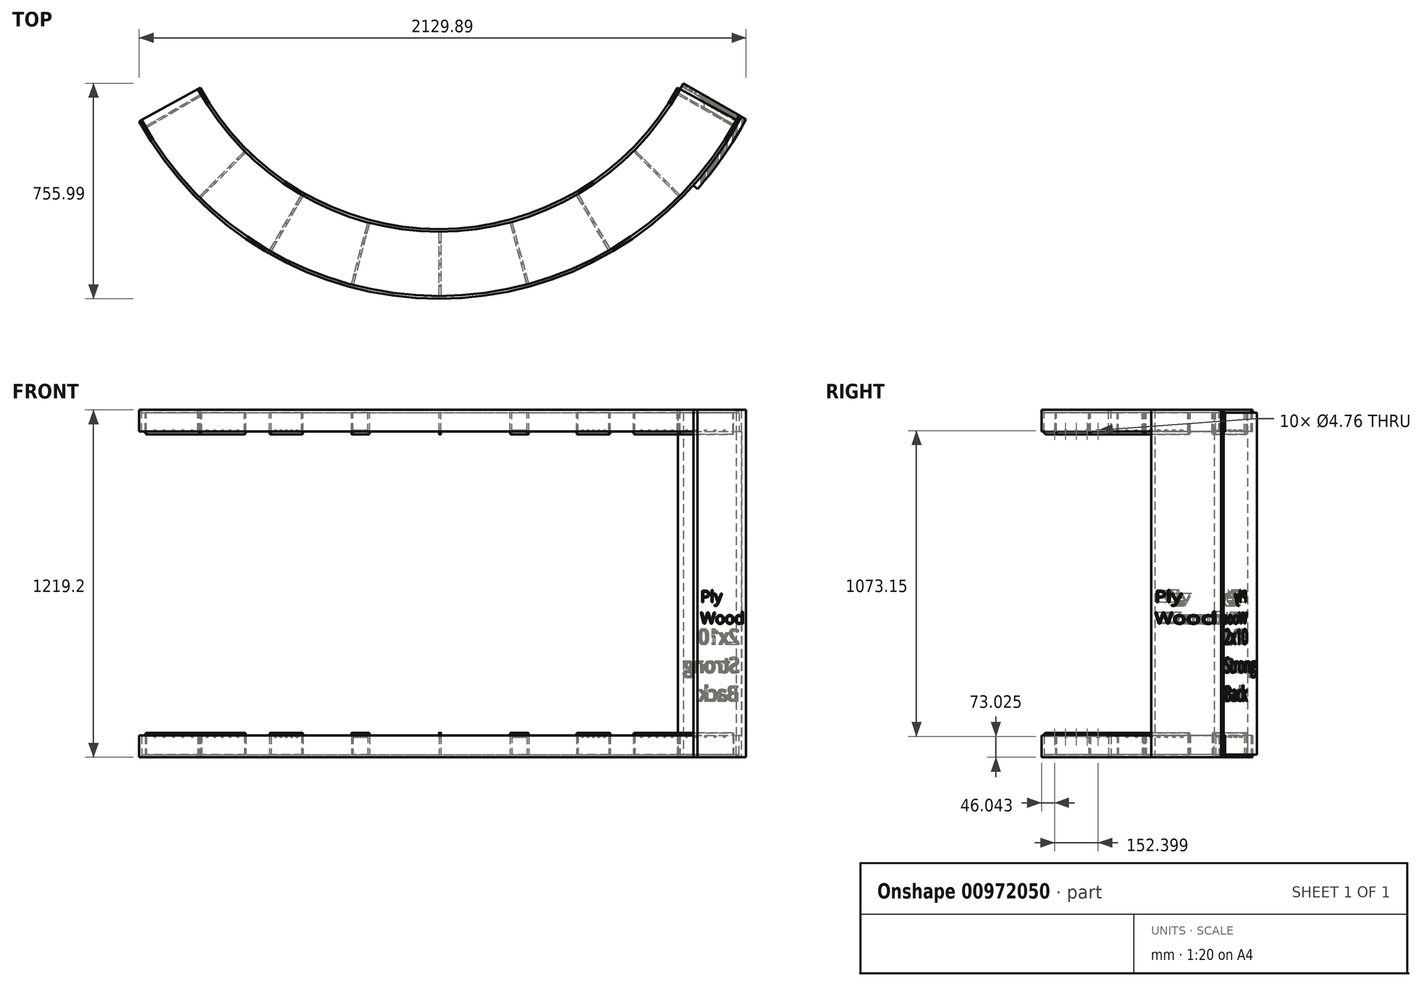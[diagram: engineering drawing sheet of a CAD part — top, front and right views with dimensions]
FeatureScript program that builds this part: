
annotation { "Feature Type Name" : "Feature", "Feature Type Description" : "" }
export const myFeature = defineFeature(function(context is Context, id is Id, definition is map)
    precondition{}
    {
        {
            var Q0;
            Q0=qCreatedBy(makeId("Top.planeOp"),FACE);
            var sketch = newSketch(context, id + "F0", { "sketchPlane" : qUnion([Q0])});
            skCircle(sketch, "E0", {"center": v(0, 0) * mm, "radius": 1190.62 * mm});
            skCircle(sketch, "E1.0", {"center": v(0, 0) * mm, "radius": 965.2 * mm});
            skLineSegment(sketch, "E2", {"start": v(-1043.85, -572.68) * mm, "end": v(0, 0) * mm});
            skLineSegment(sketch, "E3", {"start": v(0, 0) * mm, "end": v(0, -1190.62) * mm, "construction": true});
            skLineSegment(sketch, "E4.MirrorCS", {"start": v(1043.85, -572.68) * mm, "end": v(0, 0) * mm});
            skSolve(sketch);
        }
        {
            var Q0;
            {var subQ0=sQuery(id+"F0.wireOp",EDGE,"E2");var subQ1=sQuery(id+"F0.wireOp",EDGE,"E0");var subQ2=makeQuery(id+"F0.imprint","INTERSECT",VERTEX,{"derivedFrom":[subQ1,subQ0]});Q0=makeQuery(id+"F0.imprint","IMPRINT",FACE,{"disambiguationData":[TD([[makeQuery(id+"F0.imprint","IMPRINT",EDGE,{"disambiguationData":[TD([[subQ2,-1.0]])],"derivedFrom":subQ1}),1.0]])]});}
            extrude(context, id + "F1", {"entities" : qUnion([Q0]), "depth" : 9.52 * mm, "offsetDistance" : 25.4 * mm});
        }
        {
            var Q0;
            Q0=qCreatedBy(makeId("Top.planeOp"),FACE);
            var sketch = newSketch(context, id + "F2", { "sketchPlane" : qUnion([Q0])});
            skArc(sketch, "E5.0", {"start": v(-1043.85, -572.68) * mm, "mid": v(0, -1190.62) * mm, "end": v(1043.85, -572.68) * mm});
            skArc(sketch, "E6.0", {"start": v(-1052.2, -577.26) * mm, "mid": v(0, -1200.15) * mm, "end": v(1052.2, -577.26) * mm});
            skLineSegment(sketch, "E7", {"start": v(-1043.85, -572.68) * mm, "end": v(-1052.2, -577.26) * mm});
            skLineSegment(sketch, "E8", {"start": v(1052.2, -577.26) * mm, "end": v(1043.85, -572.68) * mm});
            skSolve(sketch);
        }
        {
            var Q0;
            Q0 = qSketchRegion(id + "F2", true);
            extrude(context, id + "F3", {"entities" : qUnion([Q0]), "depth" : 76.2 * mm, "offsetDistance" : 25.4 * mm});
        }
        {
            var Q0;
            Q0=qCreatedBy(makeId("Top.planeOp"),FACE);
            var sketch = newSketch(context, id + "F4", { "sketchPlane" : qUnion([Q0])});
            skArc(sketch, "E9.0", {"start": v(-846.22, -464.25) * mm, "mid": v(0, -965.2) * mm, "end": v(846.22, -464.25) * mm});
            skArc(sketch, "E10.0", {"start": v(-837.87, -459.67) * mm, "mid": v(0, -955.68) * mm, "end": v(837.87, -459.67) * mm});
            skLineSegment(sketch, "E11", {"start": v(-846.22, -464.25) * mm, "end": v(-837.87, -459.67) * mm});
            skLineSegment(sketch, "E12", {"start": v(846.22, -464.25) * mm, "end": v(837.87, -459.67) * mm});
            skSolve(sketch);
        }
        {
            var Q0;
            Q0 = qSketchRegion(id + "F4", true);
            extrude(context, id + "F5", {"entities" : qUnion([Q0]), "depth" : 76.2 * mm, "offsetDistance" : 25.4 * mm});
        }
        {
            var Q0;
            Q0=makeQuery(id+"F1.opExtrude","CAP_FACE",FACE,{"disambiguationData":[OSD([sQuery(id+"F0.wireOp",EDGE,"E0"),sQuery(id+"F0.wireOp",EDGE,"E1.0"),sQuery(id+"F0.wireOp",EDGE,"E2"),sQuery(id+"F0.wireOp",EDGE,"E4.MirrorCS")])],"isStart":false});
            var sketch = newSketch(context, id + "F6", { "sketchPlane" : qUnion([Q0])});
            skLineSegment(sketch, "E13", {"start": v(838.98, -477.21) * mm, "end": v(1034.56, -589.3) * mm});
            skLineSegment(sketch, "E14", {"start": v(1034.56, -589.3) * mm, "end": v(1031.4, -594.82) * mm});
            skLineSegment(sketch, "E15", {"start": v(1031.4, -594.82) * mm, "end": v(835.82, -482.72) * mm});
            skLineSegment(sketch, "E16", {"start": v(835.82, -482.72) * mm, "end": v(838.98, -477.21) * mm});
            skLineSegment(sketch, "E17", {"start": v(837.4, -479.97) * mm, "end": v(1032.98, -592.06) * mm, "construction": true});
            skSolve(sketch);
        }
        {
            var Q0;
            Q0 = qSketchRegion(id + "F6", true);
            extrude(context, id + "F7", {"entities" : qUnion([Q0]), "depth" : 76.2 * mm, "offsetDistance" : 25.4 * mm});
        }
        {
            var Q0;
            Q0=makeQuery(id+"F1.opExtrude","CAP_FACE",FACE,{"disambiguationData":[OSD([sQuery(id+"F0.wireOp",EDGE,"E0"),sQuery(id+"F0.wireOp",EDGE,"E1.0"),sQuery(id+"F0.wireOp",EDGE,"E2"),sQuery(id+"F0.wireOp",EDGE,"E4.MirrorCS")])],"isStart":false});
            var sketch = newSketch(context, id + "F8", { "sketchPlane" : qUnion([Q0])});
            skLineSegment(sketch, "E18.0", {"start": v(857.93, -444.16) * mm, "end": v(1061.77, -560.99) * mm});
            skLineSegment(sketch, "E19.0", {"start": v(838.98, -477.21) * mm, "end": v(1042.82, -594.04) * mm});
            skLineSegment(sketch, "E20", {"start": v(838.98, -477.21) * mm, "end": v(857.93, -444.16) * mm});
            skPoint(sketch, "E21.orphan", {"position": v(1034.56, -589.3) * mm});
            skLineSegment(sketch, "E22", {"start": v(1042.82, -594.04) * mm, "end": v(1061.77, -560.99) * mm});
            skSolve(sketch);
        }
        {
            var Q0;
            Q0 = qSketchRegion(id + "F8", true);
            extrude(context, id + "F9", {"entities" : qUnion([Q0]), "depth" : 1200.15 * mm, "offsetDistance" : 25.4 * mm});
        }
        {
            var Q0;
            Q0=makeQuery(id+"F9.opExtrude","SWEPT_FACE",FACE,{"disambiguationData":[OSD([sQuery(id+"F8.wireOp",EDGE,"E18.0")])]});
            var sketch = newSketch(context, id + "F10", { "sketchPlane" : qUnion([Q0])});
            skLineSegment(sketch, "E23.bottom", {"start": v(-1200.15, 9.53) * mm, "end": v(-1190.42, 9.53) * mm});
            skLineSegment(sketch, "E23.top", {"start": v(-1200.15, 76.2) * mm, "end": v(-1190.42, 76.2) * mm});
            skLineSegment(sketch, "E23.left", {"start": v(-1200.15, 9.52) * mm, "end": v(-1200.15, 76.2) * mm});
            skLineSegment(sketch, "E23.right", {"start": v(-1190.42, 9.53) * mm, "end": v(-1190.42, 76.2) * mm});
            skLineSegment(sketch, "E24", {"start": v(-1200.15, 609.6) * mm, "end": v(-965.2, 609.6) * mm, "construction": true});
            skLineSegment(sketch, "E25.MirrorCS", {"start": v(-1200.15, 1209.68) * mm, "end": v(-1190.42, 1209.68) * mm});
            skLineSegment(sketch, "E26.MirrorCS", {"start": v(-1200.15, 1143) * mm, "end": v(-1190.42, 1143) * mm});
            skLineSegment(sketch, "E27.MirrorCS", {"start": v(-1200.15, 1209.68) * mm, "end": v(-1200.15, 1143) * mm});
            skLineSegment(sketch, "E28.MirrorCS", {"start": v(-1190.42, 1209.68) * mm, "end": v(-1190.42, 1143) * mm});
            skSolve(sketch);
        }
        {
            var Q0;
            Q0 = qSketchRegion(id + "F10", true);
            var Q1;
            Q1=makeQuery(id+"F9.opExtrude","SWEPT_FACE",FACE,{"disambiguationData":[OSD([sQuery(id+"F8.wireOp",EDGE,"E19.0")])]});
            extrude(context, id + "F11", {"entities" : qUnion([Q0]), "operationType" : NewBodyOperationType.REMOVE, "endBound" : BoundingType.UP_TO_SURFACE, "oppositeDirection" : true, "depth" : 25.4 * mm, "endBoundEntityFace" : qUnion([Q1]), "offsetDistance" : 25.4 * mm});
        }
        {
            var Q0;
            Q0=makeQuery(id+"F7.opExtrude","CAP_EDGE",EDGE,{"disambiguationData":[OSD([sQuery(id+"F6.wireOp",EDGE,"E14")])],"isStart":false});
            var Q1;
            Q1=makeQuery(id+"F7.opExtrude","CAP_EDGE",EDGE,{"disambiguationData":[OSD([sQuery(id+"F6.wireOp",EDGE,"E16")])],"isStart":false});
            fillet(context, id + "F12", {"entities" : qUnion([Q0, Q1]), "radius" : 6.35 * mm, "tangentPropagation" : true, "allowEdgeOverflow" : false});
        }
        {
            var Q0;
            Q0=makeQuery(id+"F7.opExtrude","SWEPT_FACE",FACE,{"disambiguationData":[OSD([sQuery(id+"F6.wireOp",EDGE,"E13")])]});
            var sketch = newSketch(context, id + "F13", { "sketchPlane" : qUnion([Q0])});
            skCircle(sketch, "E29", {"center": v(-1154.11, 73.03) * mm, "radius": 2.38 * mm});
            skCircle(sketch, "E30", {"center": v(-1116.01, 73.03) * mm, "radius": 2.38 * mm});
            skCircle(sketch, "E31", {"center": v(-1039.81, 73.03) * mm, "radius": 2.38 * mm});
            skCircle(sketch, "E32", {"center": v(-1001.71, 73.03) * mm, "radius": 2.38 * mm});
            skLineSegment(sketch, "E33", {"start": v(-1154.11, 73.02) * mm, "end": v(-1116.01, 73.02) * mm, "construction": true});
            skLineSegment(sketch, "E34", {"start": v(-1039.81, 73.02) * mm, "end": v(-1001.71, 73.02) * mm, "construction": true});
            skLineSegment(sketch, "E35", {"start": v(-1077.91, 73.03) * mm, "end": v(-1077.91, 85.73) * mm, "construction": true});
            skCircle(sketch, "E36", {"center": v(-1077.91, 73.03) * mm, "radius": 2.38 * mm});
            skLineSegment(sketch, "E37", {"start": v(-1116.01, 73.03) * mm, "end": v(-1077.91, 73.03) * mm, "construction": true});
            skLineSegment(sketch, "E38", {"start": v(-1077.91, 73.03) * mm, "end": v(-1039.81, 73.03) * mm, "construction": true});
            skSolve(sketch);
        }
        {
            var Q0;
            Q0 = qSketchRegion(id + "F13", true);
            extrude(context, id + "F14", {"entities" : qUnion([Q0]), "operationType" : NewBodyOperationType.REMOVE, "endBound" : BoundingType.UP_TO_NEXT, "oppositeDirection" : true, "depth" : 25.4 * mm, "offsetDistance" : 25.4 * mm});
        }
        {
            var Q0;
            Q0=makeQuery(id+"F7.opExtrude","SWEPT_BODY",BODY,{"disambiguationData":[OSD([sQuery(id+"F6.wireOp",EDGE,"E13"),sQuery(id+"F6.wireOp",EDGE,"E14"),sQuery(id+"F6.wireOp",EDGE,"E15"),sQuery(id+"F6.wireOp",EDGE,"E16")])]});
            var Q1;
            Q1=makeQuery(id+"F5.opExtrude","SWEPT_FACE",FACE,{"disambiguationData":[OSD([sQuery(id+"F4.wireOp",EDGE,"E10.0")])]});
            circularPattern(context, id + "F15", {"entities" : qUnion([Q0]), "axis" : qUnion([Q1]), "angle" : 120 * degree, "instanceCount" : 9, "oppositeDirection" : true, "equalSpace" : true});
        }
        {
            var Q0;
            Q0=qCreatedBy(makeId("Top.planeOp"),FACE);
            var sketch = newSketch(context, id + "F16", { "sketchPlane" : qUnion([Q0])});
            skArc(sketch, "E39.0", {"start": v(907, -814.75) * mm, "mid": v(999.85, -697.67) * mm, "end": v(1077.7, -570.11) * mm});
            skLineSegment(sketch, "E40", {"start": v(1077.7, -570.11) * mm, "end": v(1061.15, -560.64) * mm});
            skArc(sketch, "E41.0", {"start": v(892.82, -802.02) * mm, "mid": v(984.41, -686.5) * mm, "end": v(1061.15, -560.64) * mm});
            skPoint(sketch, "E42.orphan", {"position": v(1052.2, -577.26) * mm});
            skLineSegment(sketch, "E43", {"start": v(907, -814.75) * mm, "end": v(892.82, -802.02) * mm});
            skPoint(sketch, "E44.orphan", {"position": v(-1052.2, -577.26) * mm});
            skSolve(sketch);
        }
        {
            var Q0;
            Q0 = qSketchRegion(id + "F16", true);
            var Q1;
            Q1=makeQuery(id+"F9.opExtrude","CAP_FACE",FACE,{"disambiguationData":[OSD([sQuery(id+"F8.wireOp",EDGE,"E18.0"),sQuery(id+"F8.wireOp",EDGE,"E19.0"),sQuery(id+"F8.wireOp",EDGE,"E20"),sQuery(id+"F8.wireOp",EDGE,"E22")])],"isStart":false});
            extrude(context, id + "F17", {"entities" : qUnion([Q0]), "depth" : 1219.2 * mm, "endBoundEntityFace" : qUnion([Q1]), "offsetDistance" : 25.4 * mm});
        }
        {
            var Q0;
            Q0=qCreatedBy(makeId("Top.planeOp"),FACE);
            cPlane(context, id + "F18", {"entities" : qUnion([Q0]), "cplaneType" : CPlaneType.OFFSET, "offset" : 609.6 * mm, "width" : 152.4 * mm, "height" : 152.4 * mm});
        }
        {
            var Q0;
            Q0=makeQuery(id+"F1.opExtrude","SWEPT_BODY",BODY,{"disambiguationData":[OSD([sQuery(id+"F0.wireOp",EDGE,"E0"),sQuery(id+"F0.wireOp",EDGE,"E1.0"),sQuery(id+"F0.wireOp",EDGE,"E2"),sQuery(id+"F0.wireOp",EDGE,"E4.MirrorCS")])]});
            var Q1;
            Q1=makeQuery(id+"F5.opExtrude","SWEPT_BODY",BODY,{"disambiguationData":[OSD([sQuery(id+"F4.wireOp",EDGE,"E9.0"),sQuery(id+"F4.wireOp",EDGE,"E10.0"),sQuery(id+"F4.wireOp",EDGE,"E11"),sQuery(id+"F4.wireOp",EDGE,"E12")])]});
            var Q2;
            Q2=makeQuery(id+"F3.opExtrude","SWEPT_BODY",BODY,{"disambiguationData":[OSD([sQuery(id+"F2.wireOp",EDGE,"E5.0"),sQuery(id+"F2.wireOp",EDGE,"E6.0"),sQuery(id+"F2.wireOp",EDGE,"E7"),sQuery(id+"F2.wireOp",EDGE,"E8")])]});
            var Q3;
            Q3=makeQuery(id+"F7.opExtrude","SWEPT_BODY",BODY,{"disambiguationData":[OSD([sQuery(id+"F6.wireOp",EDGE,"E13"),sQuery(id+"F6.wireOp",EDGE,"E14"),sQuery(id+"F6.wireOp",EDGE,"E15"),sQuery(id+"F6.wireOp",EDGE,"E16")])]});
            var Q4;
            Q4=makeQuery(id+"F15.opPattern","COPY",BODY,{"derivedFrom":makeQuery(id+"F7.opExtrude","SWEPT_BODY",BODY,{"disambiguationData":[OSD([sQuery(id+"F6.wireOp",EDGE,"E13"),sQuery(id+"F6.wireOp",EDGE,"E14"),sQuery(id+"F6.wireOp",EDGE,"E15"),sQuery(id+"F6.wireOp",EDGE,"E16")])]}),"instanceName":"1"});
            var Q5;
            Q5=makeQuery(id+"F15.opPattern","COPY",BODY,{"derivedFrom":makeQuery(id+"F7.opExtrude","SWEPT_BODY",BODY,{"disambiguationData":[OSD([sQuery(id+"F6.wireOp",EDGE,"E13"),sQuery(id+"F6.wireOp",EDGE,"E14"),sQuery(id+"F6.wireOp",EDGE,"E15"),sQuery(id+"F6.wireOp",EDGE,"E16")])]}),"instanceName":"2"});
            var Q6;
            Q6=makeQuery(id+"F15.opPattern","COPY",BODY,{"derivedFrom":makeQuery(id+"F7.opExtrude","SWEPT_BODY",BODY,{"disambiguationData":[OSD([sQuery(id+"F6.wireOp",EDGE,"E13"),sQuery(id+"F6.wireOp",EDGE,"E14"),sQuery(id+"F6.wireOp",EDGE,"E15"),sQuery(id+"F6.wireOp",EDGE,"E16")])]}),"instanceName":"3"});
            var Q7;
            Q7=makeQuery(id+"F15.opPattern","COPY",BODY,{"derivedFrom":makeQuery(id+"F7.opExtrude","SWEPT_BODY",BODY,{"disambiguationData":[OSD([sQuery(id+"F6.wireOp",EDGE,"E13"),sQuery(id+"F6.wireOp",EDGE,"E14"),sQuery(id+"F6.wireOp",EDGE,"E15"),sQuery(id+"F6.wireOp",EDGE,"E16")])]}),"instanceName":"4"});
            var Q8;
            Q8=makeQuery(id+"F15.opPattern","COPY",BODY,{"derivedFrom":makeQuery(id+"F7.opExtrude","SWEPT_BODY",BODY,{"disambiguationData":[OSD([sQuery(id+"F6.wireOp",EDGE,"E13"),sQuery(id+"F6.wireOp",EDGE,"E14"),sQuery(id+"F6.wireOp",EDGE,"E15"),sQuery(id+"F6.wireOp",EDGE,"E16")])]}),"instanceName":"5"});
            var Q9;
            Q9=makeQuery(id+"F15.opPattern","COPY",BODY,{"derivedFrom":makeQuery(id+"F7.opExtrude","SWEPT_BODY",BODY,{"disambiguationData":[OSD([sQuery(id+"F6.wireOp",EDGE,"E13"),sQuery(id+"F6.wireOp",EDGE,"E14"),sQuery(id+"F6.wireOp",EDGE,"E15"),sQuery(id+"F6.wireOp",EDGE,"E16")])]}),"instanceName":"6"});
            var Q10;
            Q10=makeQuery(id+"F15.opPattern","COPY",BODY,{"derivedFrom":makeQuery(id+"F7.opExtrude","SWEPT_BODY",BODY,{"disambiguationData":[OSD([sQuery(id+"F6.wireOp",EDGE,"E13"),sQuery(id+"F6.wireOp",EDGE,"E14"),sQuery(id+"F6.wireOp",EDGE,"E15"),sQuery(id+"F6.wireOp",EDGE,"E16")])]}),"instanceName":"7"});
            var Q11;
            Q11=makeQuery(id+"F15.opPattern","COPY",BODY,{"derivedFrom":makeQuery(id+"F7.opExtrude","SWEPT_BODY",BODY,{"disambiguationData":[OSD([sQuery(id+"F6.wireOp",EDGE,"E13"),sQuery(id+"F6.wireOp",EDGE,"E14"),sQuery(id+"F6.wireOp",EDGE,"E15"),sQuery(id+"F6.wireOp",EDGE,"E16")])]}),"instanceName":"8"});
            var Q12;
            Q12=qCreatedBy(id+"F18.planeOp",FACE);
            mirror(context, id + "F19", {"entities" : qUnion([Q0, Q1, Q2, Q3, Q4, Q5, Q6, Q7, Q8, Q9, Q10, Q11]), "mirrorPlane" : qUnion([Q12])});
        }
        {
            var Q0;
            Q0=makeQuery(id+"F9.opExtrude","SWEPT_FACE",FACE,{"disambiguationData":[OSD([sQuery(id+"F8.wireOp",EDGE,"E18.0")])]});
            var sketch = newSketch(context, id + "F20", { "sketchPlane" : qUnion([Q0])});
            skText(sketch, "E45", { "text": "2x10\nStrong\nBack", "fontName": "OpenSans-Regular.ttf"});
            const initialGuessF20  = {"E45": [-1.1938, 0.39685, 1, 0, 0.0528]};
            skSetInitialGuess(sketch, initialGuessF20);
            skSolve(sketch);
        }
        {
            var Q0;
            Q0 = qSketchRegion(id + "F20", true);
            extrude(context, id + "F21", {"entities" : qUnion([Q0]), "operationType" : NewBodyOperationType.REMOVE, "oppositeDirection" : true, "depth" : 12.7 * mm, "offsetDistance" : 25.4 * mm});
        }
        {
            var Q0;
            Q0=qCreatedBy(makeId("Front.planeOp"),FACE);
            cPlane(context, id + "F22", {"entities" : qUnion([Q0]), "cplaneType" : CPlaneType.OFFSET, "offset" : 1219.2 * mm, "width" : 152.4 * mm, "height" : 152.4 * mm});
        }
        {
            var Q0;
            Q0=qCreatedBy(id+"F22.planeOp",FACE);
            var sketch = newSketch(context, id + "F23", { "sketchPlane" : qUnion([Q0])});
            skText(sketch, "E46", { "text": "Ply\nWood", "fontName": "OpenSans-Regular.ttf"});
            const initialGuessF23  = {"E46": [0.91797, 0.54438, 1, 0, 0.04026]};
            skSetInitialGuess(sketch, initialGuessF23);
            skSolve(sketch);
        }
        {
            var Q0;
            Q0 = qSketchRegion(id + "F23", true);
            extrude(context, id + "F24", {"entities" : qUnion([Q0]), "operationType" : NewBodyOperationType.REMOVE, "oppositeDirection" : true, "depth" : 762 * mm, "offsetDistance" : 25.4 * mm});
        }
    });
